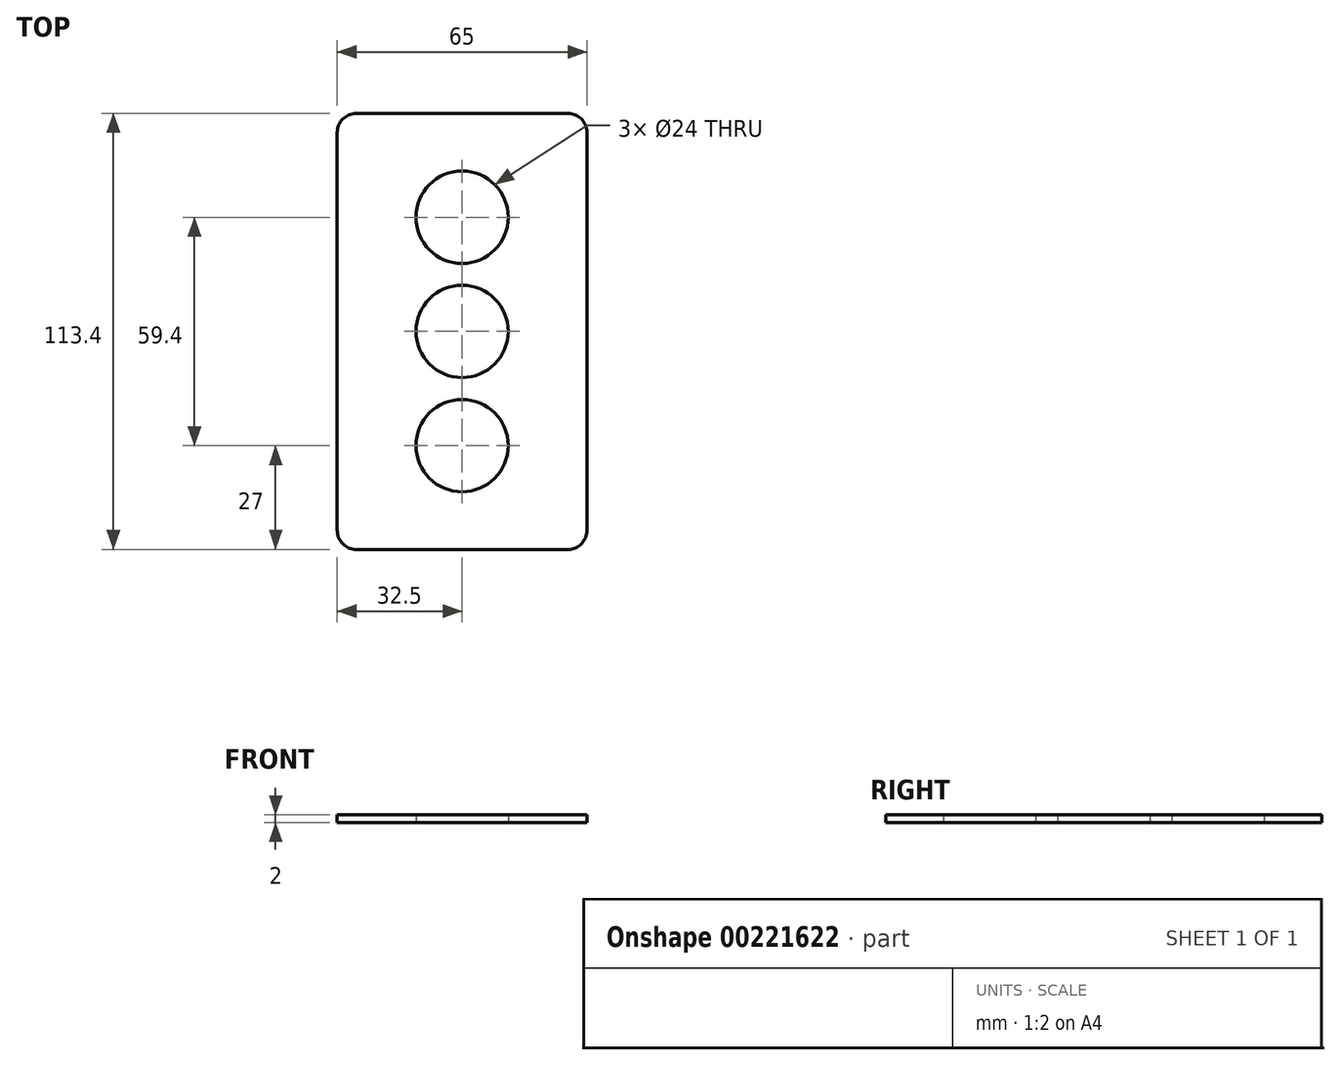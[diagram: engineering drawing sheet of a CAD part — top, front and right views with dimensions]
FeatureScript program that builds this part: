
annotation { "Feature Type Name" : "Feature", "Feature Type Description" : "" }
export const myFeature = defineFeature(function(context is Context, id is Id, definition is map)
    precondition{}
    {
        {
            var Q0;
            Q0=qCreatedBy(makeId("Top.planeOp"),FACE);
            var sketch = newSketch(context, id + "F0", { "sketchPlane" : qUnion([Q0])});
            skPoint(sketch, "E0.middle", {"position": v(0, 0) * mm});
            skCircle(sketch, "E1", {"center": v(0, 29.7) * mm, "radius": 12 * mm});
            skCircle(sketch, "E2", {"center": v(0, 0) * mm, "radius": 12 * mm});
            skCircle(sketch, "E3", {"center": v(0, -29.7) * mm, "radius": 12 * mm});
            skLineSegment(sketch, "E4.bottom", {"start": v(-32.5, 56.7) * mm, "end": v(32.5, 56.7) * mm});
            skLineSegment(sketch, "E4.top", {"start": v(-32.5, -56.7) * mm, "end": v(32.5, -56.7) * mm});
            skLineSegment(sketch, "E4.left", {"start": v(-32.5, 56.7) * mm, "end": v(-32.5, -56.7) * mm});
            skLineSegment(sketch, "E4.right", {"start": v(32.5, 56.7) * mm, "end": v(32.5, -56.7) * mm});
            skSolve(sketch);
        }
        {
            var Q0;
            Q0=makeQuery(id+"F0.imprint","IMPRINT",FACE,{"disambiguationData":[TD([[makeQuery(id+"F0.imprint","IMPRINT",EDGE,{"derivedFrom":sQuery(id+"F0.wireOp",EDGE,"E1")}),-1.0]])]});
            extrude(context, id + "F1", {"entities" : qUnion([Q0]), "depth" : 2 * mm, "offsetDistance" : 25 * mm});
        }
        {
            var Q0;
            Q0=makeQuery(id+"F1.opExtrude","SWEPT_EDGE",EDGE,{"disambiguationData":[OSD([sQuery(id+"F0.wireOp",EDGE,"E4.bottom"),sQuery(id+"F0.wireOp",EDGE,"E4.left")])]});
            var Q1;
            Q1=makeQuery(id+"F1.opExtrude","SWEPT_EDGE",EDGE,{"disambiguationData":[OSD([sQuery(id+"F0.wireOp",EDGE,"E4.bottom"),sQuery(id+"F0.wireOp",EDGE,"E4.right")])]});
            var Q2;
            Q2=makeQuery(id+"F1.opExtrude","SWEPT_EDGE",EDGE,{"disambiguationData":[OSD([sQuery(id+"F0.wireOp",EDGE,"E4.top"),sQuery(id+"F0.wireOp",EDGE,"E4.right")])]});
            var Q3;
            Q3=makeQuery(id+"F1.opExtrude","SWEPT_EDGE",EDGE,{"disambiguationData":[OSD([sQuery(id+"F0.wireOp",EDGE,"E4.top"),sQuery(id+"F0.wireOp",EDGE,"E4.left")])]});
            fillet(context, id + "F2", {"entities" : qUnion([Q0, Q1, Q2, Q3]), "tangentPropagation" : true, "radius" : 5 * mm, "defaultsChanged" : false, "vertexSettings" : [], "allowEdgeOverflow" : false});
        }
    });
